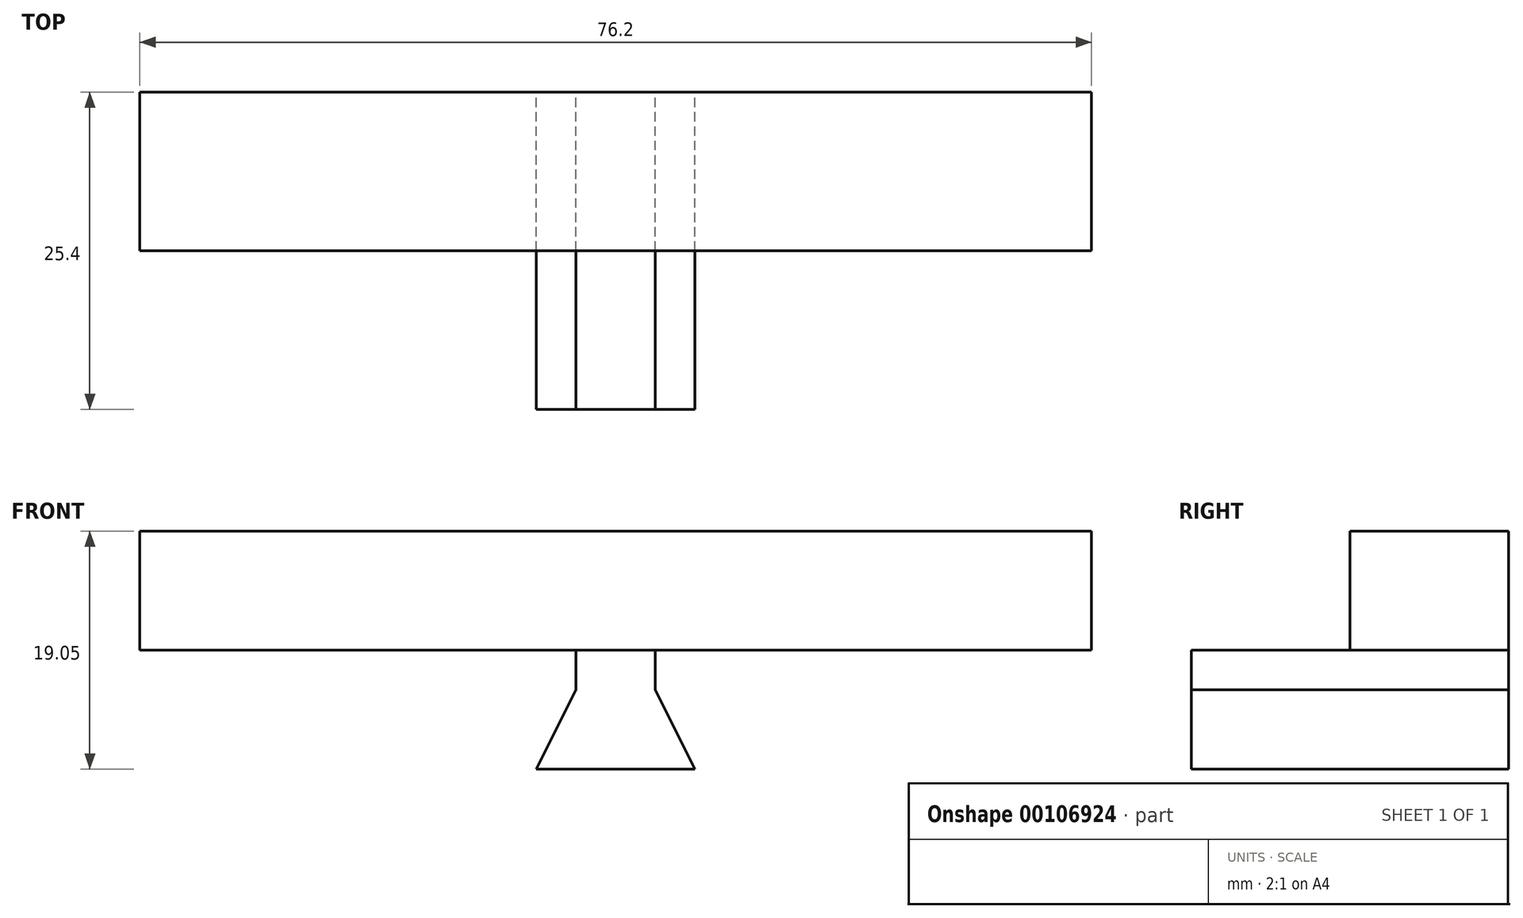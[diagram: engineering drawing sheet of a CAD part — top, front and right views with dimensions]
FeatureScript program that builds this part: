
annotation { "Feature Type Name" : "Feature", "Feature Type Description" : "" }
export const myFeature = defineFeature(function(context is Context, id is Id, definition is map)
    precondition{}
    {
        {
            var Q0;
            Q0=qCreatedBy(makeId("Front.planeOp"),FACE);
            var sketch = newSketch(context, id + "F0", { "sketchPlane" : qUnion([Q0])});
            skLineSegment(sketch, "E0", {"start": v(0, 0) * mm, "end": v(-6.35, 0) * mm});
            skLineSegment(sketch, "E1", {"start": v(-6.35, 0) * mm, "end": v(0, 0) * mm});
            skLineSegment(sketch, "E2", {"start": v(0, 0) * mm, "end": v(6.35, 0) * mm});
            skLineSegment(sketch, "E3", {"start": v(-3.17, 6.35) * mm, "end": v(-6.35, 0) * mm});
            skLineSegment(sketch, "E4", {"start": v(3.18, 6.35) * mm, "end": v(6.35, 0) * mm});
            skLineSegment(sketch, "E5", {"start": v(-3.17, 6.35) * mm, "end": v(-3.17, 9.53) * mm});
            skLineSegment(sketch, "E6", {"start": v(3.18, 6.35) * mm, "end": v(3.18, 9.53) * mm});
            skLineSegment(sketch, "E7", {"start": v(3.18, 9.53) * mm, "end": v(-3.17, 9.53) * mm});
            skPoint(sketch, "E8.start.orphan", {"position": v(0, 6.35) * mm});
            skSolve(sketch);
        }
        {
            var Q0;
            Q0 = qSketchRegion(id + "F0", true);
            extrude(context, id + "F1", {"entities" : qUnion([Q0]), "depth" : 25.4 * mm});
        }
        {
            var Q0;
            Q0=makeQuery(id+"F1.opExtrude","SWEPT_FACE",FACE,{"disambiguationData":[OSD([sQuery(id+"F0.wireOp",EDGE,"E7")])]});
            var sketch = newSketch(context, id + "F2", { "sketchPlane" : qUnion([Q0])});
            skLineSegment(sketch, "E9", {"start": v(0, 0) * mm, "end": v(-38.1, 0) * mm});
            skLineSegment(sketch, "E10", {"start": v(-38.1, 0) * mm, "end": v(-38.1, -12.7) * mm});
            skLineSegment(sketch, "E11", {"start": v(-38.1, -12.7) * mm, "end": v(0, -12.7) * mm});
            skLineSegment(sketch, "E12.MirrorCS", {"start": v(38.1, -12.7) * mm, "end": v(0, -12.7) * mm});
            skLineSegment(sketch, "E13.MirrorCS", {"start": v(0, 0) * mm, "end": v(38.1, 0) * mm});
            skLineSegment(sketch, "E14.MirrorCS", {"start": v(38.1, 0) * mm, "end": v(38.1, -12.7) * mm});
            skSolve(sketch);
        }
        {
            var Q0;
            Q0 = qSketchRegion(id + "F2", true);
            extrude(context, id + "F3", {"entities" : qUnion([Q0]), "operationType" : NewBodyOperationType.ADD, "depth" : 9.52 * mm});
        }
    });
